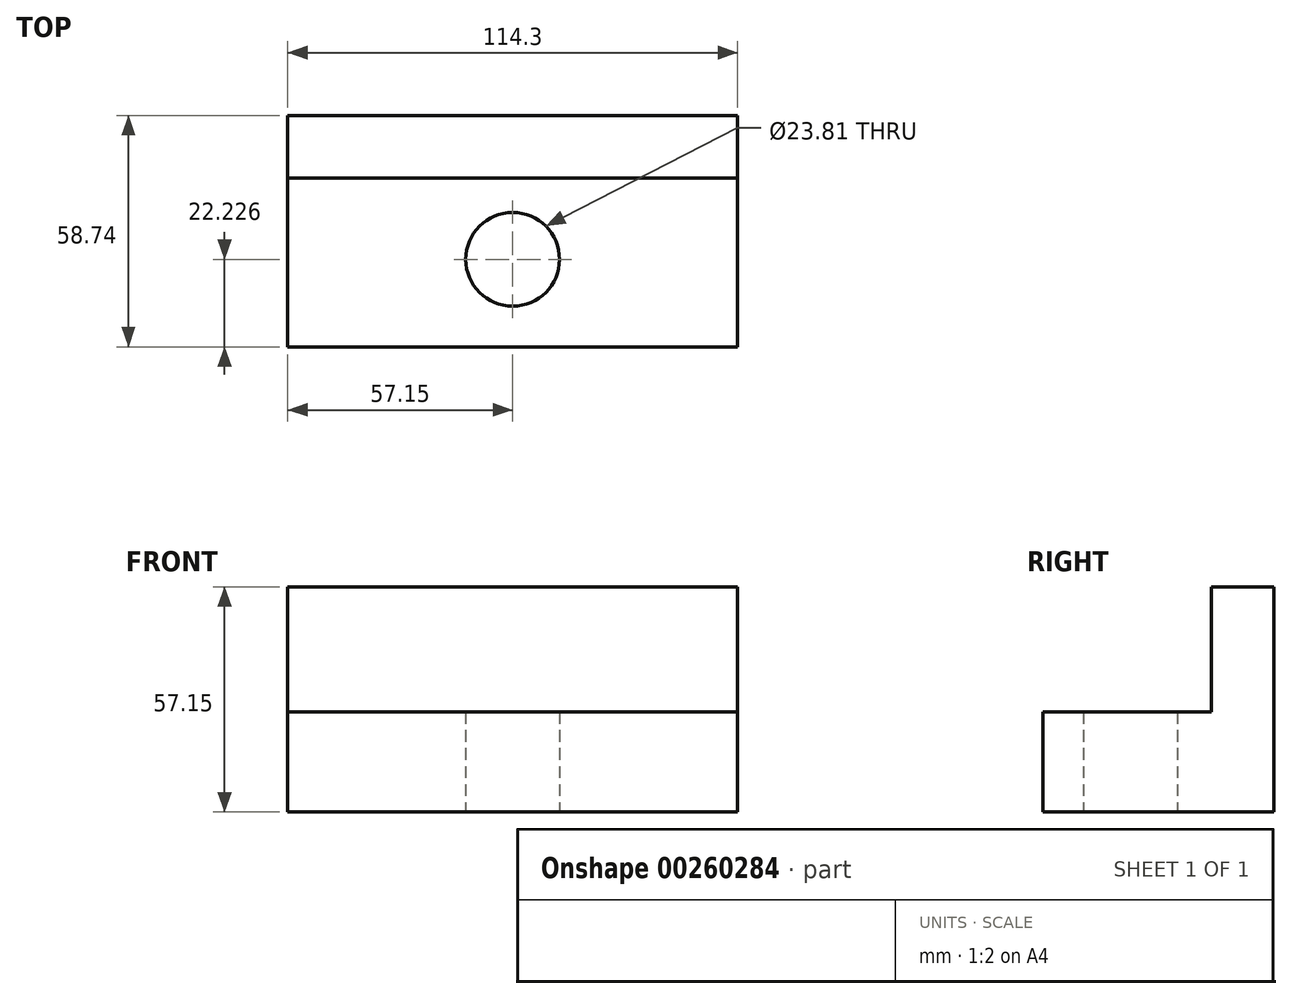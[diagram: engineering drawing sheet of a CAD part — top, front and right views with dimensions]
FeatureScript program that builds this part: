
annotation { "Feature Type Name" : "Feature", "Feature Type Description" : "" }
export const myFeature = defineFeature(function(context is Context, id is Id, definition is map)
    precondition{}
    {
        {
            var Q0;
            Q0=qCreatedBy(makeId("Top.planeOp"),FACE);
            var sketch = newSketch(context, id + "F0", { "sketchPlane" : qUnion([Q0])});
            skLineSegment(sketch, "E0.bottom", {"start": v(57.15, -29.37) * mm, "end": v(-57.15, -29.37) * mm});
            skLineSegment(sketch, "E0.top", {"start": v(57.15, 29.37) * mm, "end": v(-57.15, 29.37) * mm});
            skLineSegment(sketch, "E0.left", {"start": v(57.15, -29.37) * mm, "end": v(57.15, 29.37) * mm});
            skLineSegment(sketch, "E0.right", {"start": v(-57.15, -29.37) * mm, "end": v(-57.15, 29.37) * mm});
            skPoint(sketch, "E0.middle", {"position": v(0, 0) * mm});
            skLineSegment(sketch, "E1", {"start": v(0, 29.37) * mm, "end": v(0, 13.5) * mm});
            skCircle(sketch, "E2", {"center": v(0, -7.14) * mm, "radius": 11.9 * mm});
            skLineSegment(sketch, "E3", {"start": v(-57.15, 13.5) * mm, "end": v(57.15, 13.5) * mm});
            skLineSegment(sketch, "E4", {"start": v(-38.1, 29.37) * mm, "end": v(-38.1, 13.5) * mm});
            skLineSegment(sketch, "E5", {"start": v(38.1, 29.37) * mm, "end": v(38.1, 13.5) * mm});
            skPoint(sketch, "E6.trimOffspring.end.orphan", {"position": v(57.15, -7.14) * mm});
            skPoint(sketch, "E7.start.orphan", {"position": v(-57.15, -7.14) * mm});
            skPoint(sketch, "E8.orphan", {"position": v(0, -29.37) * mm});
            skSolve(sketch);
        }
        {
            var Q0;
            {var subQ1=sQuery(id+"F0.wireOp",EDGE,"E0.bottom");Q0=makeQuery(id+"F0.imprint","IMPRINT",FACE,{"disambiguationData":[TD([[makeQuery(id+"F0.imprint","IMPRINT",EDGE,{"derivedFrom":subQ1}),-1.0]])]});}
            extrude(context, id + "F1", {"entities" : qUnion([Q0]), "depth" : 25.4 * mm});
        }
        {
            var Q0;
            {var subQ3=sQuery(id+"F0.wireOp",EDGE,"E4");Q0=makeQuery(id+"F0.imprint","IMPRINT",FACE,{"disambiguationData":[TD([[makeQuery(id+"F0.imprint","IMPRINT",EDGE,{"derivedFrom":subQ3}),-1.0]])]});}
            var Q1;
            {var subQ0=sQuery(id+"F0.wireOp",EDGE,"E1");Q1=makeQuery(id+"F0.imprint","IMPRINT",FACE,{"disambiguationData":[TD([[makeQuery(id+"F0.imprint","IMPRINT",EDGE,{"derivedFrom":subQ0}),-1.0]])]});}
            var Q2;
            {var subQ0=sQuery(id+"F0.wireOp",EDGE,"E1");Q2=makeQuery(id+"F0.imprint","IMPRINT",FACE,{"disambiguationData":[TD([[makeQuery(id+"F0.imprint","IMPRINT",EDGE,{"derivedFrom":subQ0}),1.0]])]});}
            var Q3;
            {var subQ3=sQuery(id+"F0.wireOp",EDGE,"E5");Q3=makeQuery(id+"F0.imprint","IMPRINT",FACE,{"disambiguationData":[TD([[makeQuery(id+"F0.imprint","IMPRINT",EDGE,{"derivedFrom":subQ3}),1.0]])]});}
            extrude(context, id + "F2", {"entities" : qUnion([Q0, Q1, Q2, Q3]), "operationType" : NewBodyOperationType.ADD, "depth" : 57.15 * mm});
        }
    });
